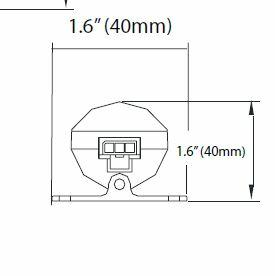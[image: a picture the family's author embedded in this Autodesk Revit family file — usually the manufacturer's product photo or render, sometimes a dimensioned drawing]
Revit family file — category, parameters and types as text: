
# Revit family: Lighting-Control-Acclaim-Al Driver 200
name_source: partatom
category: Lighting Fixtures
revit_build: Autodesk Revit 2016 (Build: 20170117_1200(x64)
units: mm (PartAtom-declared; Revit-internal decimal feet)

## family parameters
Cut with Voids When Loaded = No
Host = Face
Light Source = No
Part Type = Normal
Room Calculation Point = No
Round Connector Dimension = Use Diameter
Shared = No

## types (1)
- Lighting-Control-Acclaim-Al Driver 200
    Apparent Load = 0 VA
    Default Elevation = 1219 mm
    Description = Driver
    Housing Finish = Aluminum
    Lamp = LED
    Length = 250 mm  [stored 0.82021 ft]
    Manufacturer = Acclaim Lighting
    Model = AL Driver 200
    Number of Poles = 1
    Power Factor = 1
    URL = http://www.acclaimlighting.com
    Voltage = 0 V
    Width = 160 mm  [stored 0.524934 ft]

note: [stored X ft] marks values corroborated as IEEE doubles in the binary element streams (Revit-internal decimal feet)

## geometry (parser evidence)
native form markers: Blend x13, Sweep x3
no freeform markers — native parametric forms only
